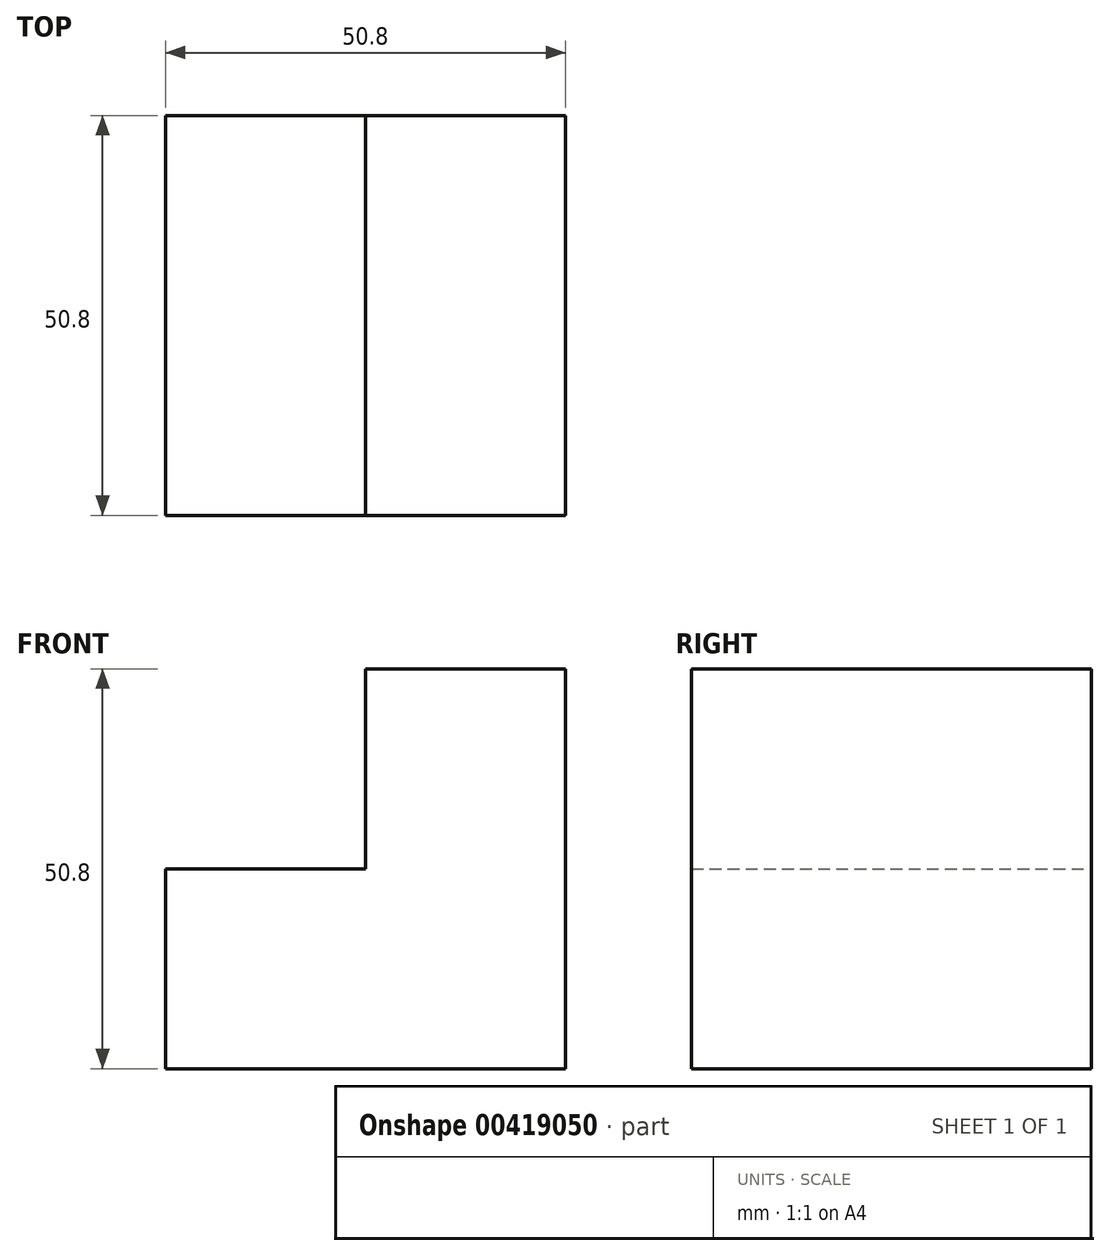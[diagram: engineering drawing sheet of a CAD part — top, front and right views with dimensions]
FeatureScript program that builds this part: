
annotation { "Feature Type Name" : "Feature", "Feature Type Description" : "" }
export const myFeature = defineFeature(function(context is Context, id is Id, definition is map)
    precondition{}
    {
        {
            var Q0;
            Q0=qCreatedBy(makeId("Front.planeOp"),FACE);
            var sketch = newSketch(context, id + "F0", { "sketchPlane" : qUnion([Q0])});
            skLineSegment(sketch, "E0", {"start": v(0, 0) * mm, "end": v(-50.8, 0) * mm});
            skLineSegment(sketch, "E1", {"start": v(0, 0) * mm, "end": v(0, 50.8) * mm});
            skLineSegment(sketch, "E2", {"start": v(0, 50.8) * mm, "end": v(-25.4, 50.8) * mm});
            skLineSegment(sketch, "E3", {"start": v(-50.8, 0) * mm, "end": v(-50.8, 25.4) * mm});
            skLineSegment(sketch, "E4", {"start": v(-50.8, 25.4) * mm, "end": v(-25.4, 25.4) * mm});
            skLineSegment(sketch, "E5", {"start": v(-25.4, 50.8) * mm, "end": v(-25.4, 25.4) * mm});
            skSolve(sketch);
        }
        {
            var Q0;
            Q0 = qSketchRegion(id + "F0", true);
            extrude(context, id + "F1", {"entities" : qUnion([Q0]), "depth" : 50.8 * mm});
        }
    });
